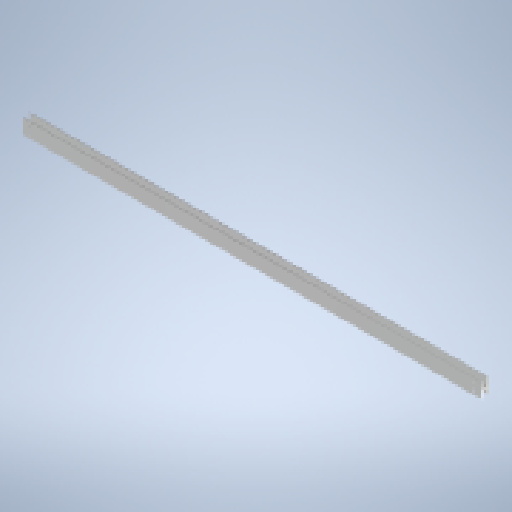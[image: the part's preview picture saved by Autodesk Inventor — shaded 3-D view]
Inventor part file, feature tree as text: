
AUTODESK INVENTOR PART (.ipt)
format: ipt  version: 2025 (Build 290162010, 162A)  size: 184,320 bytes
history: native  units: mm
features: sketch x2, other x1, extrude x1, hole x1
ambient origin geometry x8: Origin, YZ Plane, XZ Plane, XY Plane, X Axis, Y Axis, Z Axis, Center Point
bodies: Body1 (feature_tree)
feature tree (5):
  other  "Träger"
  extrude  "Extrusion1"  Depth=1.5mm
  hole  "Bohrung1"  [1 undecoded]
  sketch  "Skizze1"  dims[d0=2.0mm d1=1.5mm]
  sketch  "Skizze2"  dims[d2=32.0mm d3=18.0mm d4=1000.0mm d5=0.0mm d6=15.0mm d8=15.0mm d9=15.0mm d10=5.0mm d11=6.0mm d12=10.4mm d13=2.0mm d14=90.0deg d15=8.0mm d16=20.594885mm d17=8.5mm d18=15.0mm]
note: 1 required parameter value undecoded (feature->parameter linkage not recoverable at this tier; creation-order binding heuristic only, values carry confidence <= 0.55)
